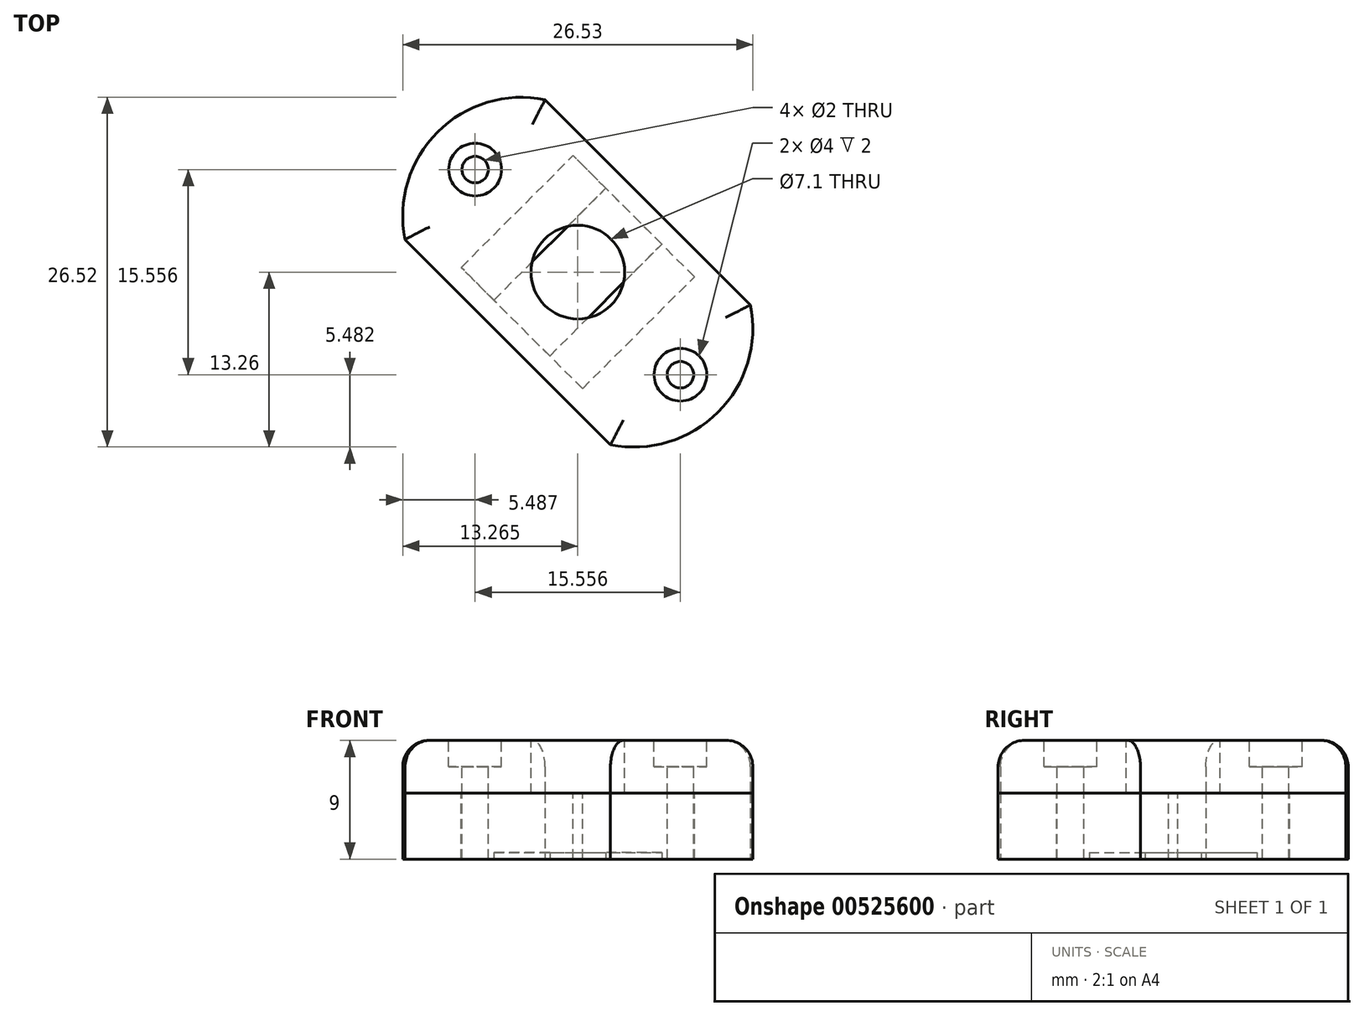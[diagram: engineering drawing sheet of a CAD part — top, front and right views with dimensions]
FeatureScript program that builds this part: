
annotation { "Feature Type Name" : "Feature", "Feature Type Description" : "" }
export const myFeature = defineFeature(function(context is Context, id is Id, definition is map)
    precondition{}
    {
        {
            var Q0;
            Q0=qCreatedBy(makeId("Top.planeOp"),FACE);
            var sketch = newSketch(context, id + "F0", { "sketchPlane" : qUnion([Q0])});
            skLineSegment(sketch, "E0.top", {"start": v(-34, -36.04) * mm, "end": v(-56, -36.04) * mm});
            skLineSegment(sketch, "E0.left", {"start": v(-34, -51.04) * mm, "end": v(-34, -36.04) * mm});
            skLineSegment(sketch, "E0.right", {"start": v(-56, -51.04) * mm, "end": v(-56, -36.04) * mm});
            skPoint(sketch, "E0.middle", {"position": v(-45, -43.54) * mm});
            skArc(sketch, "E1", {"start": v(-34, -51.04) * mm, "mid": v(-29.97, -43.54) * mm, "end": v(-34, -36.04) * mm});
            skArc(sketch, "E2", {"start": v(-56, -36.04) * mm, "mid": v(-60.03, -43.54) * mm, "end": v(-56, -51.04) * mm});
            skLineSegment(sketch, "E3", {"start": v(-56, -51.04) * mm, "end": v(-34, -51.04) * mm});
            skSolve(sketch);
        }
        {
            var Q0;
            Q0=qSketchRegion(id+"F0",true);
            extrude(context, id + "F1", {"entities" : qUnion([Q0]), "depth" : 5 * mm, "offsetDistance" : 25 * mm});
        }
        {
            var Q0;
            Q0=makeQuery(id+"F1.opExtrude","CAP_FACE",FACE,{"disambiguationData":[OSD([sQuery(id+"F0.wireOp",EDGE,"E0.bottom"),sQuery(id+"F0.wireOp",EDGE,"E0.top"),sQuery(id+"F0.wireOp",EDGE,"E0.left"),sQuery(id+"F0.wireOp",EDGE,"E0.right")])],"isStart":false});
            var sketch = newSketch(context, id + "F2", { "sketchPlane" : qUnion([Q0])});
            skCircle(sketch, "E4", {"center": v(-56, -43.54) * mm, "radius": 1 * mm});
            skCircle(sketch, "E5", {"center": v(-34, -43.54) * mm, "radius": 1 * mm});
            skCircle(sketch, "E6", {"center": v(-45, -43.54) * mm, "radius": 3.55 * mm, "construction": true});
            skLineSegment(sketch, "E7.bottom", {"start": v(-38.5, -49.54) * mm, "end": v(-51.5, -49.54) * mm});
            skLineSegment(sketch, "E7.top", {"start": v(-38.5, -37.54) * mm, "end": v(-51.5, -37.54) * mm});
            skLineSegment(sketch, "E7.left", {"start": v(-38.5, -49.54) * mm, "end": v(-38.5, -37.54) * mm});
            skLineSegment(sketch, "E7.right", {"start": v(-51.5, -49.54) * mm, "end": v(-51.5, -37.54) * mm});
            skSolve(sketch);
        }
        {
            var Q0;
            Q0=qSketchRegion(id+"F2",true);
            extrude(context, id + "F3", {"entities" : qUnion([Q0]), "operationType" : NewBodyOperationType.REMOVE, "oppositeDirection" : true, "depth" : 5 * mm});
        }
        {
            var Q0;
            Q0=makeQuery(id+"F1.opExtrude","CAP_FACE",FACE,{"disambiguationData":[OSD([sQuery(id+"F0.wireOp",EDGE,"E0.top"),sQuery(id+"F0.wireOp",EDGE,"E1"),sQuery(id+"F0.wireOp",EDGE,"E2"),sQuery(id+"F0.wireOp",EDGE,"E3")])],"isStart":true});
            var sketch = newSketch(context, id + "F4", { "sketchPlane" : qUnion([Q0])});
            skPoint(sketch, "E8.middle.positionSnap0", {"position": v(-45, 37.54) * mm});
            skPoint(sketch, "E8.centerSnap0", {"position": v(-45, 37.54) * mm});
            skLineSegment(sketch, "E9.bottom", {"start": v(-42, 49.54) * mm, "end": v(-48, 49.54) * mm});
            skLineSegment(sketch, "E9.top", {"start": v(-42, 37.54) * mm, "end": v(-48, 37.54) * mm});
            skLineSegment(sketch, "E9.left", {"start": v(-42, 49.54) * mm, "end": v(-42, 37.54) * mm});
            skLineSegment(sketch, "E9.right", {"start": v(-48, 49.54) * mm, "end": v(-48, 37.54) * mm});
            skPoint(sketch, "E9.middle", {"position": v(-45, 43.54) * mm});
            skPoint(sketch, "E9.middle.positionSnap0", {"position": v(-38.5, 43.54) * mm});
            skPoint(sketch, "E9.centerSnap0", {"position": v(-38.5, 43.54) * mm});
            skSolve(sketch);
        }
        {
            var Q0;
            Q0 = qSketchRegion(id + "F4", true);
            extrude(context, id + "F5", {"entities" : qUnion([Q0]), "operationType" : NewBodyOperationType.ADD, "oppositeDirection" : true, "depth" : 0.5 * mm, "offsetDistance" : 25 * mm});
        }
        {
            var Q0;
            Q0=makeQuery(id+"F1.opExtrude","CAP_FACE",FACE,{"disambiguationData":[OSD([sQuery(id+"F0.wireOp",EDGE,"E0.top"),sQuery(id+"F0.wireOp",EDGE,"E1"),sQuery(id+"F0.wireOp",EDGE,"E2"),sQuery(id+"F0.wireOp",EDGE,"E3")])],"isStart":false});
            var sketch = newSketch(context, id + "F6", { "sketchPlane" : qUnion([Q0])});
            skLineSegment(sketch, "E10.top", {"start": v(-34, -36.04) * mm, "end": v(-56, -36.04) * mm});
            skLineSegment(sketch, "E10.left", {"start": v(-34, -51.04) * mm, "end": v(-34, -36.04) * mm});
            skLineSegment(sketch, "E10.right", {"start": v(-56, -51.04) * mm, "end": v(-56, -36.04) * mm});
            skPoint(sketch, "E10.middle", {"position": v(-45, -43.54) * mm});
            skArc(sketch, "E11", {"start": v(-34, -51.04) * mm, "mid": v(-29.97, -43.54) * mm, "end": v(-34, -36.04) * mm});
            skArc(sketch, "E12", {"start": v(-56, -36.04) * mm, "mid": v(-60.03, -43.54) * mm, "end": v(-56, -51.04) * mm});
            skLineSegment(sketch, "E13", {"start": v(-56, -51.04) * mm, "end": v(-34, -51.04) * mm});
            skPoint(sketch, "E14", {"position": v(-38.5, -43.54) * mm});
            skPoint(sketch, "E15", {"position": v(-45, -37.54) * mm});
            skSolve(sketch);
        }
        {
            var Q0;
            Q0 = qSketchRegion(id + "F6", true);
            extrude(context, id + "F7", {"entities" : qUnion([Q0]), "depth" : 4 * mm, "offsetDistance" : 25 * mm});
        }
        {
            var Q0;
            Q0=makeQuery(id+"F7.opExtrude","CAP_FACE",FACE,{"disambiguationData":[OSD([sQuery(id+"F6.wireOp",EDGE,"E10.top"),sQuery(id+"F6.wireOp",EDGE,"E11"),sQuery(id+"F6.wireOp",EDGE,"E12"),sQuery(id+"F6.wireOp",EDGE,"E13")])],"isStart":false});
            var sketch = newSketch(context, id + "F8", { "sketchPlane" : qUnion([Q0])});
            skCircle(sketch, "E16", {"center": v(-56, -43.54) * mm, "radius": 1 * mm, "construction": true});
            skCircle(sketch, "E17", {"center": v(-34, -43.54) * mm, "radius": 1 * mm, "construction": true});
            skCircle(sketch, "E18", {"center": v(-45, -43.54) * mm, "radius": 3.55 * mm});
            skPoint(sketch, "E19", {"position": v(-29.97, -43.54) * mm});
            skPoint(sketch, "E20", {"position": v(-45, -51.04) * mm});
            skSolve(sketch);
        }
        {
            var Q0;
            Q0 = qSketchRegion(id + "F8", true);
            extrude(context, id + "F9", {"entities" : qUnion([Q0]), "operationType" : NewBodyOperationType.REMOVE, "oppositeDirection" : true, "depth" : 4 * mm, "offsetDistance" : 25 * mm});
        }
        {
            var Q0;
            Q0=makeQuery(id+"F7.opExtrude","CAP_EDGE",EDGE,{"disambiguationData":[OSD([sQuery(id+"F6.wireOp",EDGE,"E11")])],"isStart":false});
            var Q1;
            Q1=makeQuery(id+"F7.opExtrude","CAP_EDGE",EDGE,{"disambiguationData":[OSD([sQuery(id+"F6.wireOp",EDGE,"E10.top")])],"isStart":false});
            var Q2;
            Q2=makeQuery(id+"F7.opExtrude","CAP_EDGE",EDGE,{"disambiguationData":[OSD([sQuery(id+"F6.wireOp",EDGE,"E12")])],"isStart":false});
            var Q3;
            Q3=makeQuery(id+"F7.opExtrude","CAP_EDGE",EDGE,{"disambiguationData":[OSD([sQuery(id+"F6.wireOp",EDGE,"E13")])],"isStart":false});
            fillet(context, id + "F10", {"entities" : qUnion([Q0, Q1, Q2, Q3]), "radius" : 2 * mm, "tangentPropagation" : true, "allowEdgeOverflow" : false});
        }
        {
            var Q0;
            Q0=sQuery(id+"F8.wireOp",VERTEX,"E17.center");
            var Q1;
            Q1=sQuery(id+"F8.wireOp",VERTEX,"E16.center");
            var Q2;
            Q2=makeQuery(id+"F7.opExtrude","SWEPT_BODY",BODY,{"disambiguationData":[OSD([sQuery(id+"F6.wireOp",EDGE,"E10.top"),sQuery(id+"F6.wireOp",EDGE,"E11"),sQuery(id+"F6.wireOp",EDGE,"E12"),sQuery(id+"F6.wireOp",EDGE,"E13")])]});
            hole(context, id + "F11", {"style" : HoleStyle.C_BORE, "endStyle" : HoleEndStyle.BLIND, "holeDiameter" : 2 * mm, "cBoreDiameter" : 4 * mm, "cBoreDepth" : 2 * mm, "majorDiameter" : 5 * mm, "holeDepth" : 20 * mm, "tappedDepth" : 12 * mm, "tapClearance" : 3, "locations" : qUnion([Q0, Q1]), "scope" : qUnion([Q2])});
        }
        {
            var Q0;
            Q0=makeQuery(id+"F1.opExtrude","SWEPT_BODY",BODY,{"disambiguationData":[OSD([sQuery(id+"F0.wireOp",EDGE,"E0.top"),sQuery(id+"F0.wireOp",EDGE,"E1"),sQuery(id+"F0.wireOp",EDGE,"E2"),sQuery(id+"F0.wireOp",EDGE,"E3")])]});
            var Q1;
            Q1=makeQuery(id+"F7.opExtrude","SWEPT_BODY",BODY,{"disambiguationData":[OSD([sQuery(id+"F6.wireOp",EDGE,"E10.top"),sQuery(id+"F6.wireOp",EDGE,"E11"),sQuery(id+"F6.wireOp",EDGE,"E12"),sQuery(id+"F6.wireOp",EDGE,"E13")])]});
            var Q2;
            Q2=makeQuery(id+"F1.opExtrude","SWEPT_EDGE",EDGE,{"disambiguationData":[OSD([sQuery(id+"F0.wireOp",EDGE,"E0.left"),sQuery(id+"F0.wireOp",EDGE,"E1"),sQuery(id+"F0.wireOp",EDGE,"E3")])]});
            transform(context, id + "F12", {"entities" : qUnion([Q0, Q1]), "transformType" : TransformType.ROTATION, "transformAxis" : qUnion([Q2]), "angle" : 45 * degree, "makeCopy" : false});
        }
    });
